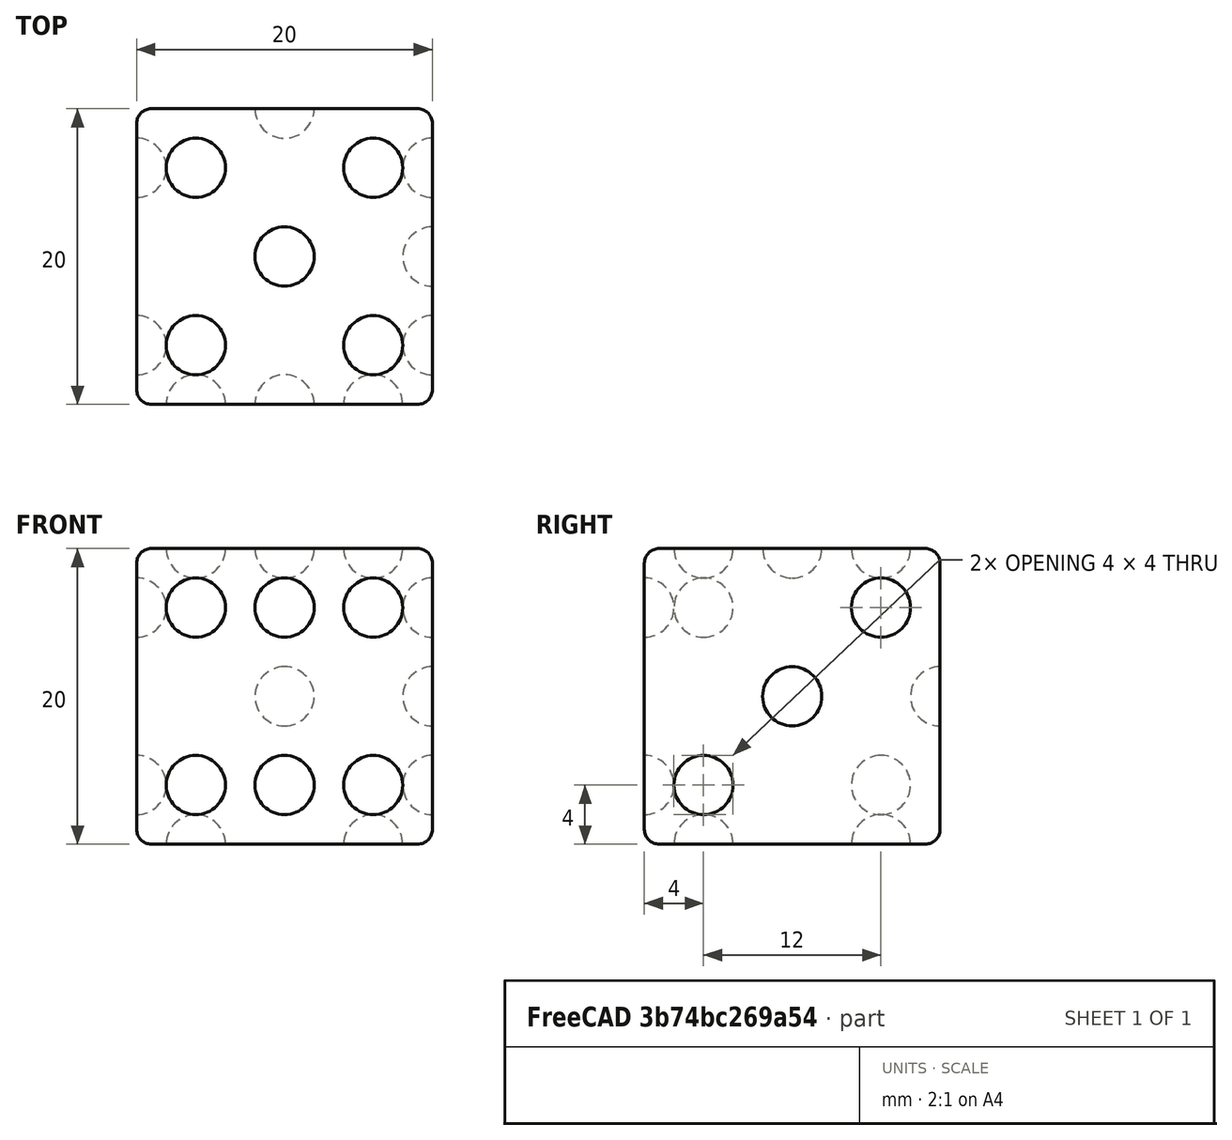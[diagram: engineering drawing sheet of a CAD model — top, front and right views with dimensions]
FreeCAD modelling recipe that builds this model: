
FCSTD DOCUMENT  (FreeCAD 1.0R39319 (Git))
Label: ojt1_t13r02_dau
License: All rights reserved
LicenseURL: https://en.wikipedia.org/wiki/All_rights_reserved
objects: Part::Sphere×10, Part::Cut×6, Part::FeaturePython×3, Part::MultiFuse×3, Part::Box×1, Part::Fillet×1
note: 24 computed .brp shape members not serialized (recipe doc carries the construction recipe); baked Part::Feature solids carry a one-line shape summary decoded from their .brp

FEATURE [Part::Box] Box  label="Cub"
  AttacherType = Attacher::AttachEngine3D
  Height = 20
  Length = 20
  Width = 20
FEATURE [Part::Fillet] Fillet
  Base = -> Box
  EdgeLinks = -> Box [Edge1,Edge2,Edge3,Edge4,Edge5,Edge6,Edge7,Edge8,Edge9,Edge10,Edge11,Edge12]
  Edges = 12 edges r=1: [Edge1,Edge2,Edge3,Edge4,Edge5,Edge6,Edge7,Edge8,Edge9,Edge10,Edge11,Edge12]
FEATURE [Part::Sphere] Sphere  label="Esfera"
  Angle1 = -90
  Angle2 = 90
  Angle3 = 360
  AttacherType = Attacher::AttachEngine3D
  Placement = pos=(4,0,4) rot=(0,0,1;0rad)
  Radius = 2
FEATURE [Part::FeaturePython] Array  label="6"  # Draft array (typed FeaturePython)
  Angle = 360
  ArrayType = 0
  Axis = (0,0,1)
  Base = -> Sphere
  Center = (0,0,0)
  Count = 6
  Fuse = false
  IntervalAxis = (0,0,0)
  IntervalX = (6,0,0)
  IntervalY = (0,14,0)
  IntervalZ = (0,0,12)
  NumberCircles = 3
  NumberPolar = 5
  NumberX = 3
  NumberY = 1
  NumberZ = 2
  RadialDistance = 50
  Symmetry = 1
  TangentialDistance = 25
FEATURE [Part::Sphere] Sphere001  label="Esfera001"
  Angle1 = -90
  Angle2 = 90
  Angle3 = 360
  AttacherType = Attacher::AttachEngine3D
  Placement = pos=(0,4,4) rot=(0,0,1;0rad)
  Radius = 2
FEATURE [Part::FeaturePython] Array001  label="4"  # Draft array (typed FeaturePython)
  Angle = 360
  ArrayType = 0
  Axis = (0,0,1)
  Base = -> Sphere001
  Center = (0,0,0)
  Count = 4
  Fuse = false
  IntervalAxis = (0,0,0)
  IntervalX = (10,0,0)
  IntervalY = (0,12,0)
  IntervalZ = (0,0,12)
  NumberCircles = 3
  NumberPolar = 5
  NumberX = 1
  NumberY = 2
  NumberZ = 2
  RadialDistance = 50
  Symmetry = 1
  TangentialDistance = 25
FEATURE [Part::Sphere] Sphere002  label="Esfera002"
  Angle1 = -90
  Angle2 = 90
  Angle3 = 360
  AttacherType = Attacher::AttachEngine3D
  Placement = pos=(10,10,20) rot=(0,0,1;0rad)
  Radius = 2
FEATURE [Part::Sphere] Sphere003  label="Esfera003"
  Angle1 = -90
  Angle2 = 90
  Angle3 = 360
  AttacherType = Attacher::AttachEngine3D
  Placement = pos=(4,4,20) rot=(0,0,1;0rad)
  Radius = 2
FEATURE [Part::FeaturePython] Array002  # Draft array (typed FeaturePython)
  Angle = 360
  ArrayType = 0
  Axis = (0,0,1)
  Base = -> Sphere003
  Center = (0,0,0)
  Count = 4
  Fuse = false
  IntervalAxis = (0,0,0)
  IntervalX = (12,0,0)
  IntervalY = (0,12,0)
  IntervalZ = (0,0,100)
  NumberCircles = 3
  NumberPolar = 5
  NumberX = 2
  NumberY = 2
  NumberZ = 1
  RadialDistance = 50
  Symmetry = 1
  TangentialDistance = 25
FEATURE [Part::Sphere] Sphere004  label="1"
  Angle1 = -90
  Angle2 = 90
  Angle3 = 360
  AttacherType = Attacher::AttachEngine3D
  Placement = pos=(10,20,10) rot=(0,0,1;0rad)
  Radius = 2
FEATURE [Part::MultiFuse] Fusion  label="5"
  Shapes = -> [Array002,Sphere002]
FEATURE [Part::Sphere] Sphere005  label="1001"
  Angle1 = -90
  Angle2 = 90
  Angle3 = 360
  AttacherType = Attacher::AttachEngine3D
  Placement = pos=(20,10,10) rot=(0,0,1;0rad)
  Radius = 2
FEATURE [Part::Sphere] Sphere006  label="1001001"
  Angle1 = -90
  Angle2 = 90
  Angle3 = 360
  AttacherType = Attacher::AttachEngine3D
  Placement = pos=(20,16,16) rot=(0,0,1;0rad)
  Radius = 2
FEATURE [Part::Sphere] Sphere007  label="1001001001"
  Angle1 = -90
  Angle2 = 90
  Angle3 = 360
  AttacherType = Attacher::AttachEngine3D
  Placement = pos=(20,4,4) rot=(0,0,1;0rad)
  Radius = 2
FEATURE [Part::MultiFuse] Fusion001  label="3"
  Shapes = -> [Sphere006,Sphere007,Sphere005]
FEATURE [Part::Sphere] Sphere008  label="1001001002"
  Angle1 = -90
  Angle2 = 90
  Angle3 = 360
  AttacherType = Attacher::AttachEngine3D
  Placement = pos=(16,4,0) rot=(0,0,1;0rad)
  Radius = 2
FEATURE [Part::Sphere] Sphere009  label="1001001002001"
  Angle1 = -90
  Angle2 = 90
  Angle3 = 360
  AttacherType = Attacher::AttachEngine3D
  Placement = pos=(4,16,0) rot=(0,0,1;0rad)
  Radius = 2
FEATURE [Part::MultiFuse] Fusion002  label="2"
  Shapes = -> [Sphere008,Sphere009]
FEATURE [Part::Cut] Cut
  Base = -> Fillet
  Tool = -> Array
FEATURE [Part::Cut] Cut001
  Base = -> Cut
  Tool = -> Fusion002
FEATURE [Part::Cut] Cut002
  Base = -> Cut001
  Tool = -> Fusion001
FEATURE [Part::Cut] Cut003
  Base = -> Cut002
  Tool = -> Fusion
FEATURE [Part::Cut] Cut004
  Base = -> Cut003
  Tool = -> Sphere004
FEATURE [Part::Cut] Cut005
  Base = -> Cut004
  Tool = -> Array001
